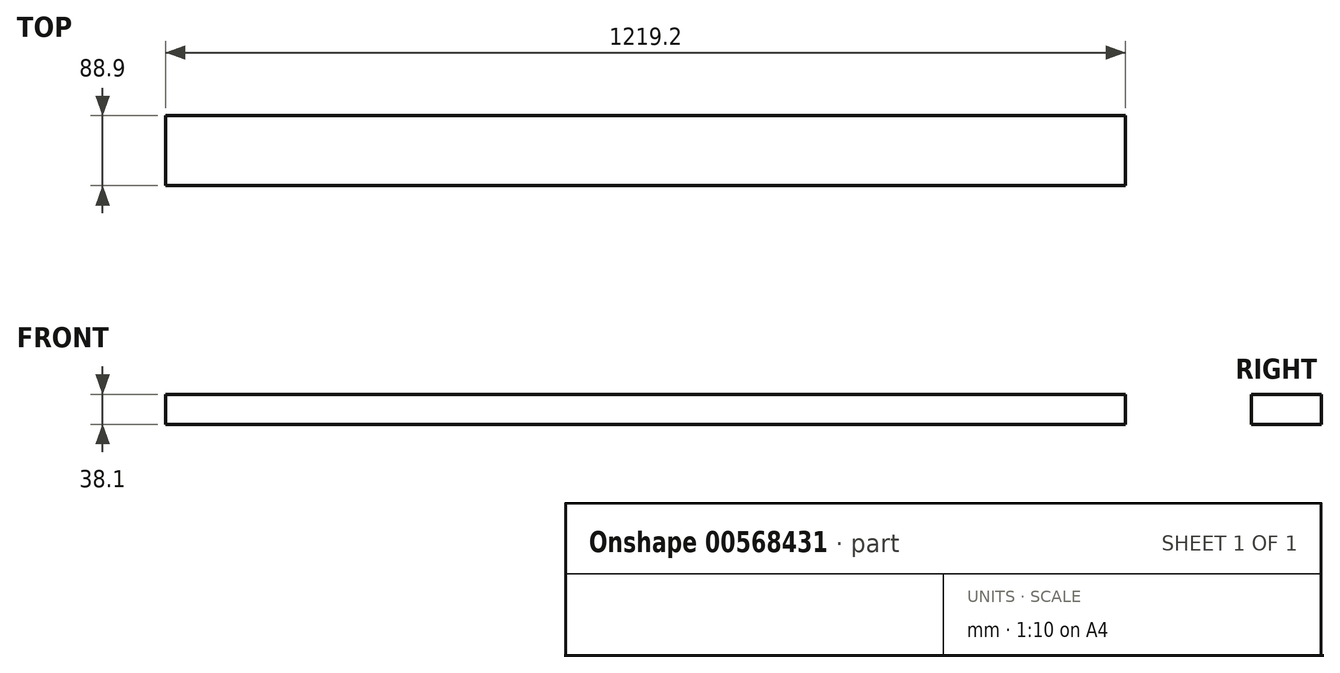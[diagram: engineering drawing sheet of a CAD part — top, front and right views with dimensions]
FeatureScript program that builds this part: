
annotation { "Feature Type Name" : "Feature", "Feature Type Description" : "" }
export const myFeature = defineFeature(function(context is Context, id is Id, definition is map)
    precondition{}
    {
        {
            var Q0;
            Q0=qCreatedBy(makeId("Front.planeOp"),FACE);
            var sketch = newSketch(context, id + "F0", { "sketchPlane" : qUnion([Q0])});
            skLineSegment(sketch, "E0", {"start": v(-1121.38, -38.1) * mm, "end": v(97.82, -38.1) * mm});
            skLineSegment(sketch, "E1", {"start": v(97.82, -38.1) * mm, "end": v(97.82, 0) * mm});
            skLineSegment(sketch, "E2", {"start": v(97.82, 0) * mm, "end": v(-1121.38, 0) * mm});
            skLineSegment(sketch, "E3", {"start": v(-1121.38, 0) * mm, "end": v(-1121.38, -38.1) * mm});
            skSolve(sketch);
        }
        {
            var Q0;
            Q0 = qSketchRegion(id + "F0", true);
            extrude(context, id + "F1", {"entities" : qUnion([Q0]), "depth" : 88.9 * mm, "offsetDistance" : 25.4 * mm});
        }
    });
